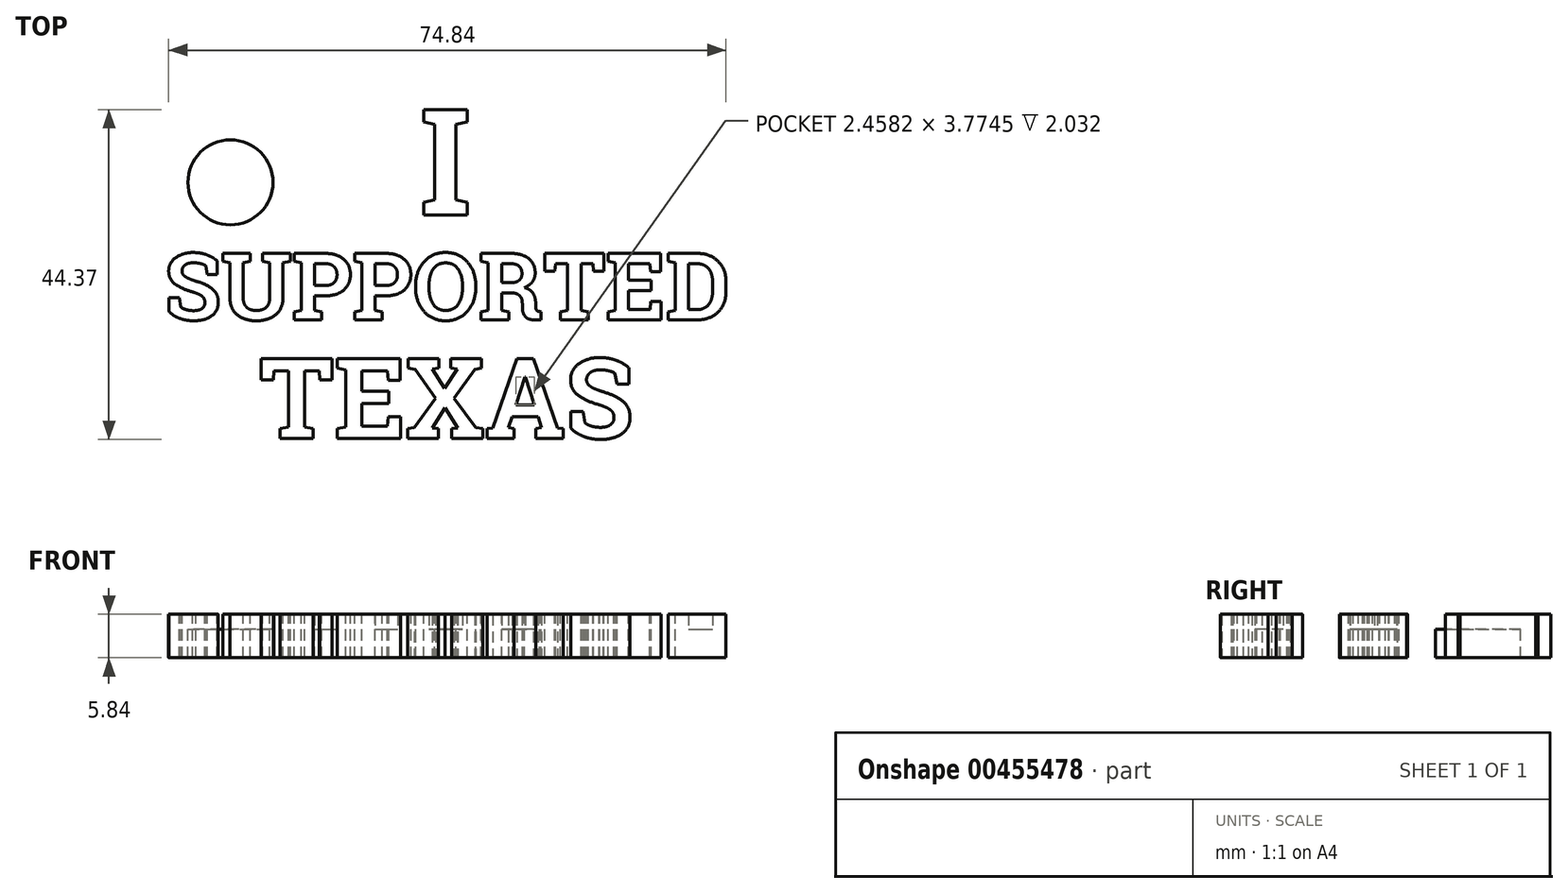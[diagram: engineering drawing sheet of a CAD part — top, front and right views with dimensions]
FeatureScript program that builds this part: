
annotation { "Feature Type Name" : "Feature", "Feature Type Description" : "" }
export const myFeature = defineFeature(function(context is Context, id is Id, definition is map)
    precondition{}
    {
        {
            var Q0;
            Q0=qCreatedBy(makeId("Top.planeOp"),FACE);
            var sketch = newSketch(context, id + "F0", { "sketchPlane" : qUnion([Q0])});
            skLineSegment(sketch, "E0.bottom", {"start": v(44.45, 25.4) * mm, "end": v(-44.45, 25.4) * mm});
            skLineSegment(sketch, "E0.top", {"start": v(44.45, -25.4) * mm, "end": v(-44.45, -25.4) * mm});
            skLineSegment(sketch, "E0.left", {"start": v(44.45, 25.4) * mm, "end": v(44.45, -25.4) * mm});
            skLineSegment(sketch, "E0.right", {"start": v(-44.45, 25.4) * mm, "end": v(-44.45, -25.4) * mm});
            skPoint(sketch, "E0.middle", {"position": v(0, 0) * mm});
            skSolve(sketch);
        }
        {
            var Q0;
            Q0=makeQuery(id+"F0.imprint","IMPRINT",FACE,{"disambiguationData":[TD([[makeQuery(id+"F0.imprint","IMPRINT",EDGE,{"derivedFrom":sQuery(id+"F0.wireOp",EDGE,"E0.bottom")}),1.0]])]});
            extrude(context, id + "F1", {"entities" : qUnion([Q0]), "depth" : 3.8 * mm});
        }
        {
            var Q0;
            Q0=makeQuery(id+"F1.opExtrude","CAP_FACE",FACE,{"disambiguationData":[OSD([sQuery(id+"F0.wireOp",EDGE,"E0.bottom"),sQuery(id+"F0.wireOp",EDGE,"E0.top"),sQuery(id+"F0.wireOp",EDGE,"E0.left"),sQuery(id+"F0.wireOp",EDGE,"E0.right")])],"isStart":false});
            var sketch = newSketch(context, id + "F2", { "sketchPlane" : qUnion([Q0])});
            skLineSegment(sketch, "E1", {"start": v(-44.45, 25.4) * mm, "end": v(-38.1, 25.4) * mm, "construction": true});
            skLineSegment(sketch, "E2", {"start": v(-38.1, 25.4) * mm, "end": v(-38.1, -25.4) * mm, "construction": true});
            skText(sketch, "E3", { "text": "SUPPORTED", "fontName": "RobotoSlab-Bold.ttf"});
            skPoint(sketch, "E4", {"position": v(0, 0) * mm});
            skText(sketch, "E5", { "text": "I", "fontName": "RobotoSlab-Bold.ttf"});
            skPoint(sketch, "E6", {"position": v(0, 16.77) * mm});
            skText(sketch, "E7", { "text": "TEXAS", "fontName": "RobotoSlab-Bold.ttf"});
            skPoint(sketch, "E8", {"position": v(0, -15.03) * mm});
            skLineSegment(sketch, "E9", {"start": v(0, 4.52) * mm, "end": v(0, 9.6) * mm, "construction": true});
            skLineSegment(sketch, "E10", {"start": v(0, -4.52) * mm, "end": v(0, -9.6) * mm, "construction": true});
            const initialGuessF2  = {"E3": [-0.0381, -0.00452, 1, 0, 0.00904], "E5": [-0.00381, 0.0096, 1, 0, 0.01434], "E7": [-0.0254, -0.02045, 1, 0, 0.01085]};
            skSetInitialGuess(sketch, initialGuessF2);
            skSolve(sketch);
        }
        {
            var Q0;
            Q0=qSketchRegion(id+"F2",true);
            extrude(context, id + "F3", {"entities" : qUnion([Q0]), "operationType" : NewBodyOperationType.ADD, "offsetDistance" : 25.4 * mm, "depth" : 2.03 * mm});
        }
        {
            var Q0;
            {var subQ0=sQuery(id+"F0.wireOp",EDGE,"E0.left");var subQ1=sQuery(id+"F0.wireOp",EDGE,"E0.bottom");var subQ2=sQuery(id+"F0.wireOp",EDGE,"E0.right");var subQ3=sQuery(id+"F0.wireOp",EDGE,"E0.top");Q0=makeQuery(id+"F3.boolean.opBoolean","SPLIT",FACE,{"disambiguationData":[TD([makeQuery(id+"F1.opExtrude","SWEPT_FACE",FACE,{"disambiguationData":[OSD([subQ1])]})])],"derivedFrom":makeQuery(id+"F1.opExtrude","CAP_FACE",FACE,{"disambiguationData":[OSD([subQ1,subQ3,subQ0,subQ2])],"isStart":false})});}
            var sketch = newSketch(context, id + "F4", { "sketchPlane" : qUnion([Q0])});
            skLineSegment(sketch, "E11.bottom", {"start": v(44.45, 25.4) * mm, "end": v(29.21, 25.4) * mm, "construction": true});
            skLineSegment(sketch, "E11.top", {"start": v(44.45, 10.16) * mm, "end": v(29.21, 10.16) * mm, "construction": true});
            skLineSegment(sketch, "E11.left", {"start": v(44.45, 25.4) * mm, "end": v(44.45, 10.16) * mm, "construction": true});
            skLineSegment(sketch, "E11.right", {"start": v(29.21, 25.4) * mm, "end": v(29.21, 10.16) * mm, "construction": true});
            skLineSegment(sketch, "E12", {"start": v(29.21, 10.16) * mm, "end": v(29.21, 13.96) * mm, "construction": true});
            skCircle(sketch, "E13.MirrorC", {"center": v(-29.21, 13.96) * mm, "radius": 5.72 * mm});
            skSolve(sketch);
        }
        {
            var Q0;
            Q0=makeQuery(id+"F4.imprint","IMPRINT",FACE,{"disambiguationData":[TD([[makeQuery(id+"F4.imprint","IMPRINT",EDGE,{"derivedFrom":sQuery(id+"F4.wireOp",EDGE,"E13.MirrorC")}),-1.0]])]});
            extrude(context, id + "F5", {"entities" : qUnion([Q0]), "operationType" : NewBodyOperationType.REMOVE, "oppositeDirection" : true, "offsetDistance" : 25.4 * mm, "depth" : 25.4 * mm});
        }
        {
            var Q0;
            {var subQ0=sQuery(id+"F0.wireOp",EDGE,"E0.left");var subQ1=sQuery(id+"F0.wireOp",EDGE,"E0.bottom");var subQ2=sQuery(id+"F0.wireOp",EDGE,"E0.right");var subQ3=sQuery(id+"F0.wireOp",EDGE,"E0.top");Q0=makeQuery(id+"F3.boolean.opBoolean","SPLIT",FACE,{"disambiguationData":[TD([makeQuery(id+"F1.opExtrude","SWEPT_FACE",FACE,{"disambiguationData":[OSD([subQ1])]})])],"derivedFrom":makeQuery(id+"F1.opExtrude","CAP_FACE",FACE,{"disambiguationData":[OSD([subQ1,subQ3,subQ0,subQ2])],"isStart":false})});}
            var sketch = newSketch(context, id + "F6", { "sketchPlane" : qUnion([Q0])});
            skLineSegment(sketch, "E14", {"start": v(-44.45, 0) * mm, "end": v(0, 25.4) * mm, "construction": true});
            skLineSegment(sketch, "E15.MirrorCS", {"start": v(20.23, 13.84) * mm, "end": v(13.25, 23.32) * mm});
            skLineSegment(sketch, "E16.MirrorCS", {"start": v(13.25, 23.32) * mm, "end": v(3.65, 23.32) * mm});
            skLineSegment(sketch, "E17.MirrorCS", {"start": v(3.65, 23.32) * mm, "end": v(4.84, 25.4) * mm});
            skLineSegment(sketch, "E18.MirrorCS", {"start": v(21.72, 16.46) * mm, "end": v(20.23, 13.84) * mm});
            skLineSegment(sketch, "E19.MirrorCS", {"start": v(25.77, 10.67) * mm, "end": v(21.72, 16.46) * mm});
            skLineSegment(sketch, "E20.MirrorCS", {"start": v(33.3, 15.95) * mm, "end": v(25.77, 10.67) * mm});
            skLineSegment(sketch, "E21.MirrorCS", {"start": v(33.3, 6.37) * mm, "end": v(33.3, 15.95) * mm});
            skLineSegment(sketch, "E22.MirrorCS", {"start": v(38.29, 9.57) * mm, "end": v(33.3, 6.37) * mm});
            skLineSegment(sketch, "E23.MirrorCS", {"start": v(44.45, 0) * mm, "end": v(38.29, 9.57) * mm});
            skLineSegment(sketch, "E24", {"start": v(4.84, 25.4) * mm, "end": v(44.45, 25.4) * mm});
            skLineSegment(sketch, "E25", {"start": v(44.45, 25.4) * mm, "end": v(44.45, 0) * mm});
            skSolve(sketch);
        }
        {
            var Q0;
            Q0=makeQuery(id+"F6.imprint","IMPRINT",FACE,{"disambiguationData":[TD([[makeQuery(id+"F6.imprint","IMPRINT",EDGE,{"derivedFrom":sQuery(id+"F6.wireOp",EDGE,"E15.MirrorCS")}),-1.0]])]});
            extrude(context, id + "F7", {"entities" : qUnion([Q0]), "operationType" : NewBodyOperationType.REMOVE, "oppositeDirection" : true, "offsetDistance" : 25.4 * mm, "depth" : 25.4 * mm});
        }
    });
